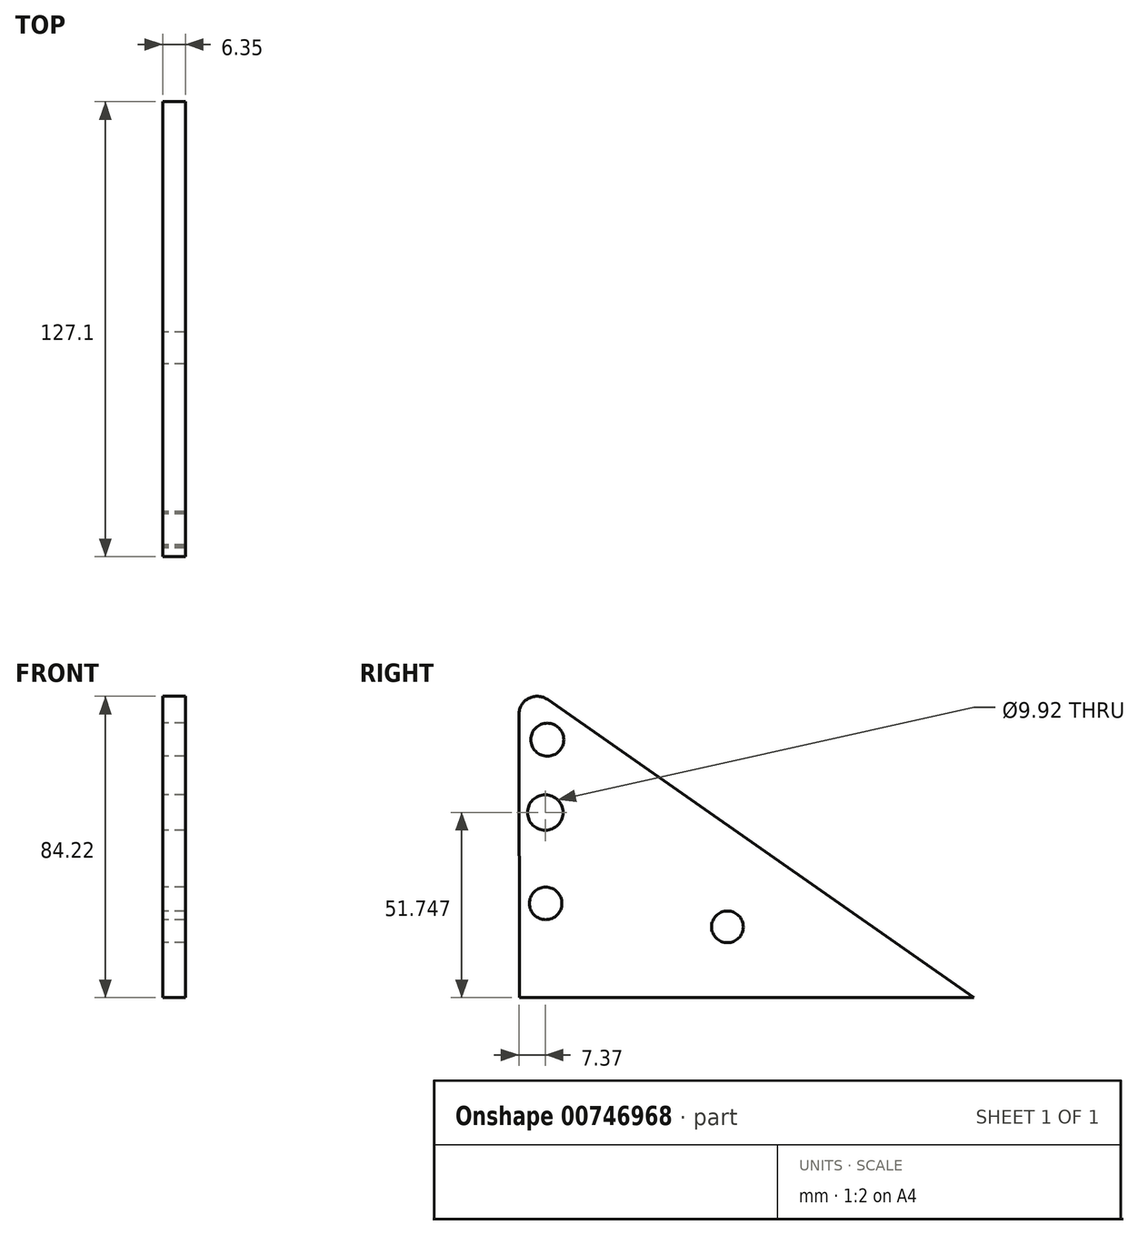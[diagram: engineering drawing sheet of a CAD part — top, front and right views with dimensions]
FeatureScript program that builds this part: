
annotation { "Feature Type Name" : "Feature", "Feature Type Description" : "" }
export const myFeature = defineFeature(function(context is Context, id is Id, definition is map)
    precondition{}
    {
        {
            var Q0;
            Q0=qCreatedBy(makeId("Right.planeOp"),FACE);
            var sketch = newSketch(context, id + "F0", { "sketchPlane" : qUnion([Q0])});
            skLineSegment(sketch, "E0", {"start": v(-36.47, 38.96) * mm, "end": v(82.64, -44.35) * mm});
            skLineSegment(sketch, "E1", {"start": v(82.64, -44.35) * mm, "end": v(-44.36, -44.35) * mm});
            skLineSegment(sketch, "E2", {"start": v(-44.36, -44.35) * mm, "end": v(-44.46, 34.79) * mm});
            skCircle(sketch, "E3", {"center": v(-36.52, 27.73) * mm, "radius": 4.61 * mm});
            skPoint(sketch, "E4.visualSharp", {"position": v(-44.48, 44.55) * mm});
            skArc(sketch, "E4.filletArc", {"start": v(-36.47, 38.96) * mm, "mid": v(-41.73, 39.3) * mm, "end": v(-44.46, 34.79) * mm});
            skCircle(sketch, "E5", {"center": v(-37.09, 7.4) * mm, "radius": 4.96 * mm});
            skCircle(sketch, "E6", {"center": v(-36.99, -18) * mm, "radius": 4.54 * mm});
            skCircle(sketch, "E7", {"center": v(13.81, -24.55) * mm, "radius": 4.43 * mm});
            skSolve(sketch);
        }
        {
            var Q0;
            Q0=makeQuery(id+"F0.imprint","IMPRINT",FACE,{"disambiguationData":[TD([[makeQuery(id+"F0.imprint","IMPRINT",EDGE,{"derivedFrom":sQuery(id+"F0.wireOp",EDGE,"E0")}),-1.0]])]});
            extrude(context, id + "F1", {"entities" : qUnion([Q0]), "depth" : 6.35 * mm, "offsetDistance" : 25.4 * mm});
        }
    });
